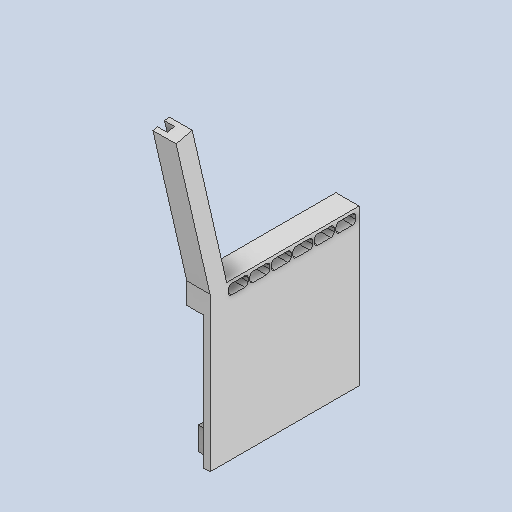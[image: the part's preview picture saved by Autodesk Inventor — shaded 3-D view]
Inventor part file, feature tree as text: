
AUTODESK INVENTOR PART (.ipt)
format: ipt  version: 2023 (Build 270158030, 158C)  size: 220,672 bytes
history: native  units: mm
features: sketch x4, other x3
ambient origin geometry x8: Origin, YZ Plane, XZ Plane, XY Plane, X Axis, Y Axis, Z Axis, Center Point
bodies: Solid1 (feature_tree)
feature tree (7):
  other  "bench-end-peice.ipt"
  other  "Solid1::bench-end-peice.ipt"
  other  "TaggingFeature1"
  sketch  "Sketch1"  dims[d0=10.0mm]
  sketch  "Sketch2"
  sketch  "Sketch3"
  sketch  "Sketch4"
